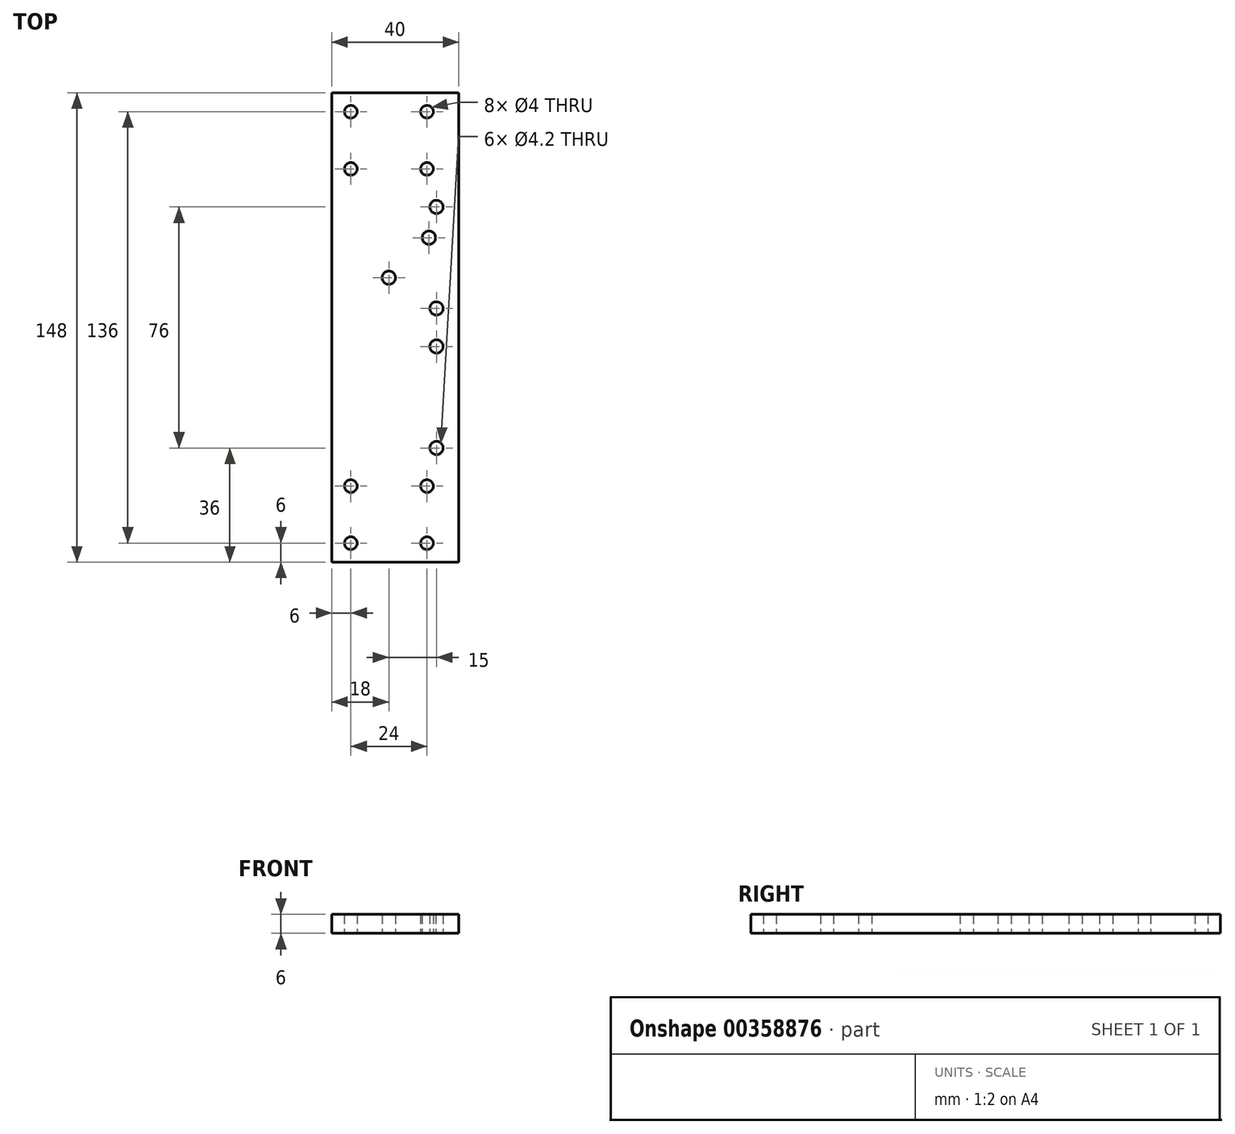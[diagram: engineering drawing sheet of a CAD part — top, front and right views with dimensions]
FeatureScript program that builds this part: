
annotation { "Feature Type Name" : "Feature", "Feature Type Description" : "" }
export const myFeature = defineFeature(function(context is Context, id is Id, definition is map)
    precondition{}
    {
        {
            var Q0;
            Q0=qCreatedBy(makeId("Top.planeOp"),FACE);
            var sketch = newSketch(context, id + "F0", { "sketchPlane" : qUnion([Q0])});
            skLineSegment(sketch, "E0.bottom", {"start": v(0, 0) * mm, "end": v(40, 0) * mm});
            skLineSegment(sketch, "E0.top", {"start": v(0, 148) * mm, "end": v(40, 148) * mm});
            skLineSegment(sketch, "E0.left", {"start": v(0, 0) * mm, "end": v(0, 148) * mm});
            skLineSegment(sketch, "E0.right", {"start": v(40, 0) * mm, "end": v(40, 148) * mm});
            skLineSegment(sketch, "E1.bottom", {"start": v(6, 6) * mm, "end": v(30, 6) * mm, "construction": true});
            skLineSegment(sketch, "E1.top", {"start": v(6, 24) * mm, "end": v(30, 24) * mm, "construction": true});
            skLineSegment(sketch, "E1.left", {"start": v(6, 6) * mm, "end": v(6, 24) * mm, "construction": true});
            skLineSegment(sketch, "E1.right", {"start": v(30, 6) * mm, "end": v(30, 24) * mm, "construction": true});
            skCircle(sketch, "E2", {"center": v(6, 24) * mm, "radius": 2 * mm});
            skCircle(sketch, "E3", {"center": v(30, 24) * mm, "radius": 2 * mm});
            skCircle(sketch, "E4", {"center": v(6, 6) * mm, "radius": 2 * mm});
            skCircle(sketch, "E5", {"center": v(30, 6) * mm, "radius": 2 * mm});
            skLineSegment(sketch, "E6.bottom", {"start": v(6, 124) * mm, "end": v(30, 124) * mm, "construction": true});
            skLineSegment(sketch, "E6.top", {"start": v(6, 142) * mm, "end": v(30, 142) * mm, "construction": true});
            skLineSegment(sketch, "E6.left", {"start": v(6, 124) * mm, "end": v(6, 142) * mm, "construction": true});
            skLineSegment(sketch, "E6.right", {"start": v(30, 124) * mm, "end": v(30, 142) * mm, "construction": true});
            skCircle(sketch, "E7", {"center": v(6, 142) * mm, "radius": 2 * mm});
            skCircle(sketch, "E8", {"center": v(30, 142) * mm, "radius": 2 * mm});
            skCircle(sketch, "E9", {"center": v(6, 124) * mm, "radius": 2 * mm});
            skCircle(sketch, "E10", {"center": v(30, 124) * mm, "radius": 2 * mm});
            skCircle(sketch, "E11", {"center": v(33, 36) * mm, "radius": 2.1 * mm});
            skCircle(sketch, "E12", {"center": v(33, 68) * mm, "radius": 2.1 * mm});
            skCircle(sketch, "E13", {"center": v(30.62, 102.31) * mm, "radius": 2.1 * mm});
            skCircle(sketch, "E14", {"center": v(18, 89.69) * mm, "radius": 2.1 * mm});
            skCircle(sketch, "E15", {"center": v(33, 80) * mm, "radius": 2.1 * mm});
            skCircle(sketch, "E16", {"center": v(33, 112) * mm, "radius": 2.1 * mm});
            skSolve(sketch);
        }
        {
            var Q0;
            Q0=makeQuery(id+"F0.imprint","IMPRINT",FACE,{"disambiguationData":[TD([[makeQuery(id+"F0.imprint","IMPRINT",EDGE,{"derivedFrom":sQuery(id+"F0.wireOp",EDGE,"E0.bottom")}),1.0]])]});
            extrude(context, id + "F1", {"entities" : qUnion([Q0]), "depth" : 6 * mm});
        }
    });
